# Revit family: MI-800
name_source: partatom
category: Pipe Accessories
revit_build: Autodesk Revit 2018 (Build: 20170223_1515(x64)
units: mm (PartAtom-declared; Revit-internal decimal feet)

## family parameters
Always vertical = Yes
Cut with Voids When Loaded = No
Part Type = Normal
Round Connector Dimension = Use Diameter
Shared = No
Work Plane-Based = No

## types (5) — shared parameters
Description = FEMALE THREADED ECCENTRIC REDUCER BUSHING
Manufacturer = MIFAB
Model = MI-800
URL = WWW.MIFAB.COM
Visible = No

## per-type parameters (varying)
| type | A-M.PT.Pipe Size | B- F.P.T. Pipe Size | C-Height | D | E |
| MI-800-2 | 0' - 3" | 0' - 2" | 0' - 0 3/4" | 0' - 0 1/4" | 0' - 2 3/4" |
| MI-800-3 | 0' - 4" | 0' - 2" | 0' - 1 1/4" | 0' - 0 3/4" | 0' - 3" |
| MI-800-4 | 0' - 4" | 0' - 3" | 0' - 1 1/4" | 0' - 0" | 0' - 3 1/2" |
| MI-800-6-4 | 0' - 6" | 0' - 4" | 0' - 1 1/4" | 0' - 0" | 0' - 4 1/4" |
| MI-800-6 | 0' - 6" | 0' - 5" | 0' - 1 1/4" | 0' - 0" | 0' - 4 1/4" |

## geometry (parser evidence)
native form markers: Sweep x3
no freeform markers — native parametric forms only
